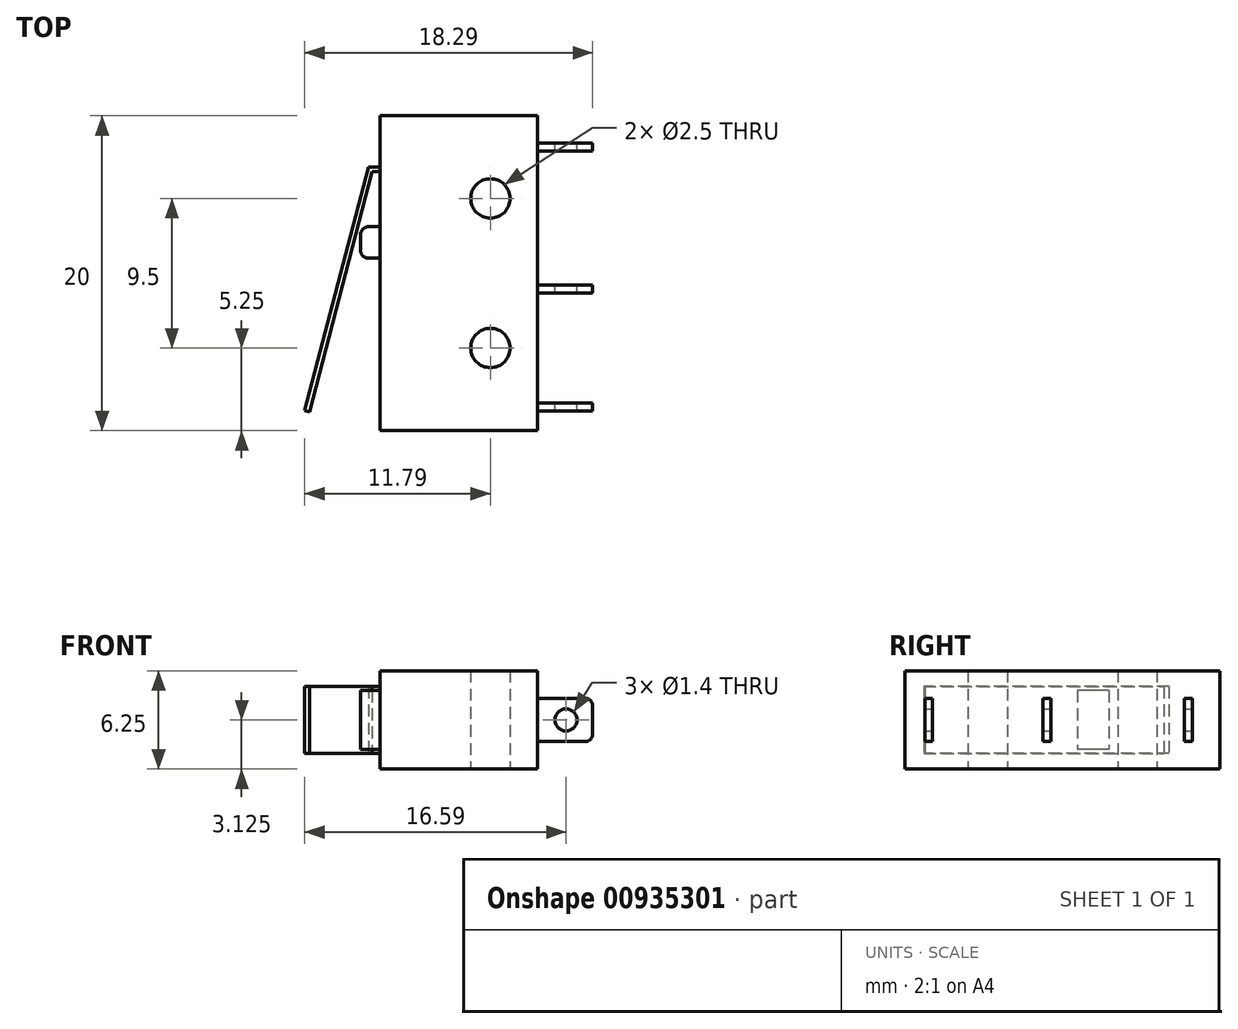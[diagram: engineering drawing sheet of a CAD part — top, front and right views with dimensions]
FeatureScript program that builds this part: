
annotation { "Feature Type Name" : "Feature", "Feature Type Description" : "" }
export const myFeature = defineFeature(function(context is Context, id is Id, definition is map)
    precondition{}
    {
        {
            var Q0;
            Q0=qCreatedBy(makeId("Top.planeOp"),FACE);
            var sketch = newSketch(context, id + "F0", { "sketchPlane" : qUnion([Q0])});
            skLineSegment(sketch, "E0.bottom", {"start": v(-5, 10) * mm, "end": v(5, 10) * mm});
            skLineSegment(sketch, "E0.top", {"start": v(-5, -10) * mm, "end": v(5, -10) * mm});
            skLineSegment(sketch, "E0.left", {"start": v(-5, 10) * mm, "end": v(-5, -10) * mm});
            skLineSegment(sketch, "E0.right", {"start": v(5, 10) * mm, "end": v(5, -10) * mm});
            skPoint(sketch, "E0.middle", {"position": v(0, 0) * mm});
            skCircle(sketch, "E1", {"center": v(2, 4.75) * mm, "radius": 1.25 * mm});
            skCircle(sketch, "E2.MirrorC", {"center": v(2, -4.75) * mm, "radius": 1.25 * mm});
            skLineSegment(sketch, "E3.bottom", {"start": v(5, 8.25) * mm, "end": v(8.5, 8.25) * mm});
            skLineSegment(sketch, "E3.top", {"start": v(5, 7.75) * mm, "end": v(8.5, 7.75) * mm});
            skLineSegment(sketch, "E3.left", {"start": v(5, 8.25) * mm, "end": v(5, 7.75) * mm});
            skLineSegment(sketch, "E3.right", {"start": v(8.5, 8.25) * mm, "end": v(8.5, 7.75) * mm});
            skLineSegment(sketch, "E4.bottom", {"start": v(5, -8.25) * mm, "end": v(8.5, -8.25) * mm});
            skLineSegment(sketch, "E4.top", {"start": v(5, -8.75) * mm, "end": v(8.5, -8.75) * mm});
            skLineSegment(sketch, "E4.left", {"start": v(5, -8.25) * mm, "end": v(5, -8.75) * mm});
            skLineSegment(sketch, "E4.right", {"start": v(8.5, -8.25) * mm, "end": v(8.5, -8.75) * mm});
            skLineSegment(sketch, "E5.bottom", {"start": v(5, -0.75) * mm, "end": v(8.5, -0.75) * mm});
            skLineSegment(sketch, "E5.top", {"start": v(5, -1.25) * mm, "end": v(8.5, -1.25) * mm});
            skLineSegment(sketch, "E5.left", {"start": v(5, -0.75) * mm, "end": v(5, -1.25) * mm});
            skLineSegment(sketch, "E5.right", {"start": v(8.5, -0.75) * mm, "end": v(8.5, -1.25) * mm});
            skLineSegment(sketch, "E6", {"start": v(-5, 6.75) * mm, "end": v(-5.73, 6.75) * mm});
            skLineSegment(sketch, "E7", {"start": v(-5.73, 6.75) * mm, "end": v(-9.8, -8.73) * mm});
            skLineSegment(sketch, "E8", {"start": v(-9.8, -8.73) * mm, "end": v(-9.5, -8.8) * mm});
            skLineSegment(sketch, "E9", {"start": v(-9.5, -8.8) * mm, "end": v(-5.5, 6.45) * mm});
            skLineSegment(sketch, "E10", {"start": v(-5.5, 6.45) * mm, "end": v(-5, 6.45) * mm});
            skLineSegment(sketch, "E11.bottom", {"start": v(-5, 2.95) * mm, "end": v(-6.25, 2.95) * mm});
            skLineSegment(sketch, "E11.top", {"start": v(-5, 0.95) * mm, "end": v(-6.25, 0.95) * mm});
            skLineSegment(sketch, "E11.left", {"start": v(-5, 2.95) * mm, "end": v(-5, 0.95) * mm});
            skLineSegment(sketch, "E11.right", {"start": v(-6.25, 2.95) * mm, "end": v(-6.25, 0.95) * mm});
            skSolve(sketch);
        }
        {
            var Q0;
            {var subQ1=sQuery(id+"F0.wireOp",EDGE,"E0.bottom");Q0=makeQuery(id+"F0.imprint","IMPRINT",FACE,{"disambiguationData":[TD([[makeQuery(id+"F0.imprint","IMPRINT",EDGE,{"derivedFrom":subQ1}),-1.0]])]});}
            extrude(context, id + "F1", {"entities" : qUnion([Q0]), "depth" : 6.25 * mm, "offsetDistance" : 25 * mm});
        }
        {
            var Q0;
            {var subQ0=sQuery(id+"F0.wireOp",EDGE,"E4.bottom");Q0=makeQuery(id+"F0.imprint","IMPRINT",FACE,{"disambiguationData":[TD([[makeQuery(id+"F0.imprint","IMPRINT",EDGE,{"derivedFrom":subQ0}),-1.0]])]});}
            var Q1;
            {var subQ2=sQuery(id+"F0.wireOp",EDGE,"E5.bottom");Q1=makeQuery(id+"F0.imprint","IMPRINT",FACE,{"disambiguationData":[TD([[makeQuery(id+"F0.imprint","IMPRINT",EDGE,{"derivedFrom":subQ2}),-1.0]])]});}
            var Q2;
            {var subQ2=sQuery(id+"F0.wireOp",EDGE,"E3.bottom");Q2=makeQuery(id+"F0.imprint","IMPRINT",FACE,{"disambiguationData":[TD([[makeQuery(id+"F0.imprint","IMPRINT",EDGE,{"derivedFrom":subQ2}),-1.0]])]});}
            var Q3;
            Q3=makeQuery(id+"F1.opExtrude","CAP_FACE",FACE,{"disambiguationData":[OSD([sQuery(id+"F0.wireOp",EDGE,"E0.bottom"),sQuery(id+"F0.wireOp",EDGE,"E0.top"),sQuery(id+"F0.wireOp",EDGE,"E0.left"),sQuery(id+"F0.wireOp",EDGE,"E0.right"),sQuery(id+"F0.wireOp",EDGE,"E1"),sQuery(id+"F0.wireOp",EDGE,"E2.MirrorC")])],"isStart":false});
            extrude(context, id + "F2", {"entities" : qUnion([Q0, Q1, Q2]), "endBound" : BoundingType.UP_TO_SURFACE, "depth" : 25 * mm, "endBoundEntityFace" : qUnion([Q3]), "hasOffset" : true, "offsetDistance" : 1.75 * mm, "hasSecondDirection" : true, "secondDirectionOppositeDirection" : false, "secondDirectionDepth" : 1.75 * mm});
        }
        {
            var Q0;
            {var subQ0=sQuery(id+"F0.wireOp",EDGE,"E6");Q0=makeQuery(id+"F0.imprint","IMPRINT",FACE,{"disambiguationData":[TD([[makeQuery(id+"F0.imprint","IMPRINT",EDGE,{"derivedFrom":subQ0}),1.0]])]});}
            var Q1;
            Q1=makeQuery(id+"F1.opExtrude","CAP_FACE",FACE,{"disambiguationData":[OSD([sQuery(id+"F0.wireOp",EDGE,"E0.bottom"),sQuery(id+"F0.wireOp",EDGE,"E0.top"),sQuery(id+"F0.wireOp",EDGE,"E0.left"),sQuery(id+"F0.wireOp",EDGE,"E0.right"),sQuery(id+"F0.wireOp",EDGE,"E1"),sQuery(id+"F0.wireOp",EDGE,"E2.MirrorC")])],"isStart":false});
            extrude(context, id + "F3", {"entities" : qUnion([Q0]), "endBound" : BoundingType.UP_TO_SURFACE, "depth" : 25 * mm, "endBoundEntityFace" : qUnion([Q1]), "hasOffset" : true, "offsetDistance" : 1 * mm, "hasSecondDirection" : true, "secondDirectionOppositeDirection" : false, "secondDirectionDepth" : 1 * mm});
        }
        {
            var Q0;
            {var subQ2=sQuery(id+"F0.wireOp",EDGE,"E11.bottom");Q0=makeQuery(id+"F0.imprint","IMPRINT",FACE,{"disambiguationData":[TD([[makeQuery(id+"F0.imprint","IMPRINT",EDGE,{"derivedFrom":subQ2}),1.0]])]});}
            var Q1;
            Q1=makeQuery(id+"F1.opExtrude","CAP_FACE",FACE,{"disambiguationData":[OSD([sQuery(id+"F0.wireOp",EDGE,"E0.bottom"),sQuery(id+"F0.wireOp",EDGE,"E0.top"),sQuery(id+"F0.wireOp",EDGE,"E0.left"),sQuery(id+"F0.wireOp",EDGE,"E0.right"),sQuery(id+"F0.wireOp",EDGE,"E1"),sQuery(id+"F0.wireOp",EDGE,"E2.MirrorC")])],"isStart":false});
            extrude(context, id + "F4", {"entities" : qUnion([Q0]), "endBound" : BoundingType.UP_TO_SURFACE, "depth" : 25 * mm, "endBoundEntityFace" : qUnion([Q1]), "hasOffset" : true, "offsetDistance" : 1.25 * mm, "hasSecondDirection" : true, "secondDirectionOppositeDirection" : false, "secondDirectionDepth" : 1.25 * mm});
        }
        {
            var Q0;
            Q0=makeQuery(id+"F4.opExtrude","SWEPT_EDGE",EDGE,{"disambiguationData":[OSD([sQuery(id+"F0.wireOp",EDGE,"E11.top"),sQuery(id+"F0.wireOp",EDGE,"E11.right")])]});
            var Q1;
            Q1=makeQuery(id+"F4.opExtrude","SWEPT_EDGE",EDGE,{"disambiguationData":[OSD([sQuery(id+"F0.wireOp",EDGE,"E11.bottom"),sQuery(id+"F0.wireOp",EDGE,"E11.right")])]});
            fillet(context, id + "F5", {"entities" : qUnion([Q0, Q1]), "radius" : .5 * mm, "tangentPropagation" : true, "allowEdgeOverflow" : false});
        }
        {
            var Q0;
            Q0=qCreatedBy(makeId("Front.planeOp"),FACE);
            var sketch = newSketch(context, id + "F6", { "sketchPlane" : qUnion([Q0])});
            skLineSegment(sketch, "E12.0", {"start": v(8.5, 4.5) * mm, "end": v(8.5, 1.75) * mm, "construction": true});
            skCircle(sketch, "E13", {"center": v(6.8, 3.12) * mm, "radius": 0.7 * mm});
            skPoint(sketch, "E13.centerSnap0", {"position": v(8.5, 3.12) * mm});
            skSolve(sketch);
        }
        {
            var Q0;
            Q0=makeQuery(id+"F6.imprint","IMPRINT",FACE,{"disambiguationData":[TD([[makeQuery(id+"F6.imprint","IMPRINT",EDGE,{"derivedFrom":sQuery(id+"F6.wireOp",EDGE,"E13")}),1.0]])]});
            extrude(context, id + "F7", {"entities" : qUnion([Q0]), "operationType" : NewBodyOperationType.REMOVE, "endBound" : BoundingType.THROUGH_ALL, "depth" : 25 * mm, "offsetDistance" : 25 * mm, "hasSecondDirection" : true, "secondDirectionBound" : SecondDirectionBoundingType.THROUGH_ALL, "secondDirectionOppositeDirection" : true, "secondDirectionDepth" : 25 * mm});
        }
        {
            var Q0;
            Q0=makeQuery(id+"F2.opExtrude","CAP_EDGE",EDGE,{"disambiguationData":[OSD([sQuery(id+"F0.wireOp",EDGE,"E4.right")])],"isStart":false});
            var Q1;
            Q1=makeQuery(id+"F2.opExtrude","CAP_EDGE",EDGE,{"disambiguationData":[OSD([sQuery(id+"F0.wireOp",EDGE,"E4.right")])],"isStart":true});
            var Q2;
            Q2=makeQuery(id+"F2.opExtrude","CAP_EDGE",EDGE,{"disambiguationData":[OSD([sQuery(id+"F0.wireOp",EDGE,"E5.right")])],"isStart":true});
            var Q3;
            Q3=makeQuery(id+"F2.opExtrude","CAP_EDGE",EDGE,{"disambiguationData":[OSD([sQuery(id+"F0.wireOp",EDGE,"E5.right")])],"isStart":false});
            var Q4;
            Q4=makeQuery(id+"F2.opExtrude","CAP_EDGE",EDGE,{"disambiguationData":[OSD([sQuery(id+"F0.wireOp",EDGE,"E3.right")])],"isStart":false});
            var Q5;
            Q5=makeQuery(id+"F2.opExtrude","CAP_EDGE",EDGE,{"disambiguationData":[OSD([sQuery(id+"F0.wireOp",EDGE,"E3.right")])],"isStart":true});
            fillet(context, id + "F8", {"entities" : qUnion([Q0, Q1, Q2, Q3, Q4, Q5]), "radius" : .5 * mm, "tangentPropagation" : true, "allowEdgeOverflow" : false});
        }
    });
